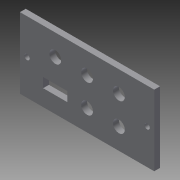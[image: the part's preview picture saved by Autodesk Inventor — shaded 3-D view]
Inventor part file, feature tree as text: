
AUTODESK INVENTOR PART (.ipt)
format: ipt  version: 2014 SP1 (Build 180222100, 222)  size: 99,840 bytes
history: native  units: in
note: dims shown in document units (in); Inventor stores cm internally (conversion verified against a paired STEP export)
features: extrude x1, sketch x1
ambient origin geometry x8: Origin, YZ Plane, XZ Plane, XY Plane, X Axis, Y Axis, Z Axis, Center Point
bodies: Solid1 (feature_tree)
feature tree (2):
  extrude  "Extrusion1"  Depth=1.25in
  sketch  "Sketch1"  dims[d0=2.375in d1=1.25in d2=0.094in d3=0.094in d4=0.43in d5=0.17in d6=0.21in d7=0.21in d8=0.21in d9=0.21in d10=0.21in d11=0.103in d12=0.0in]
